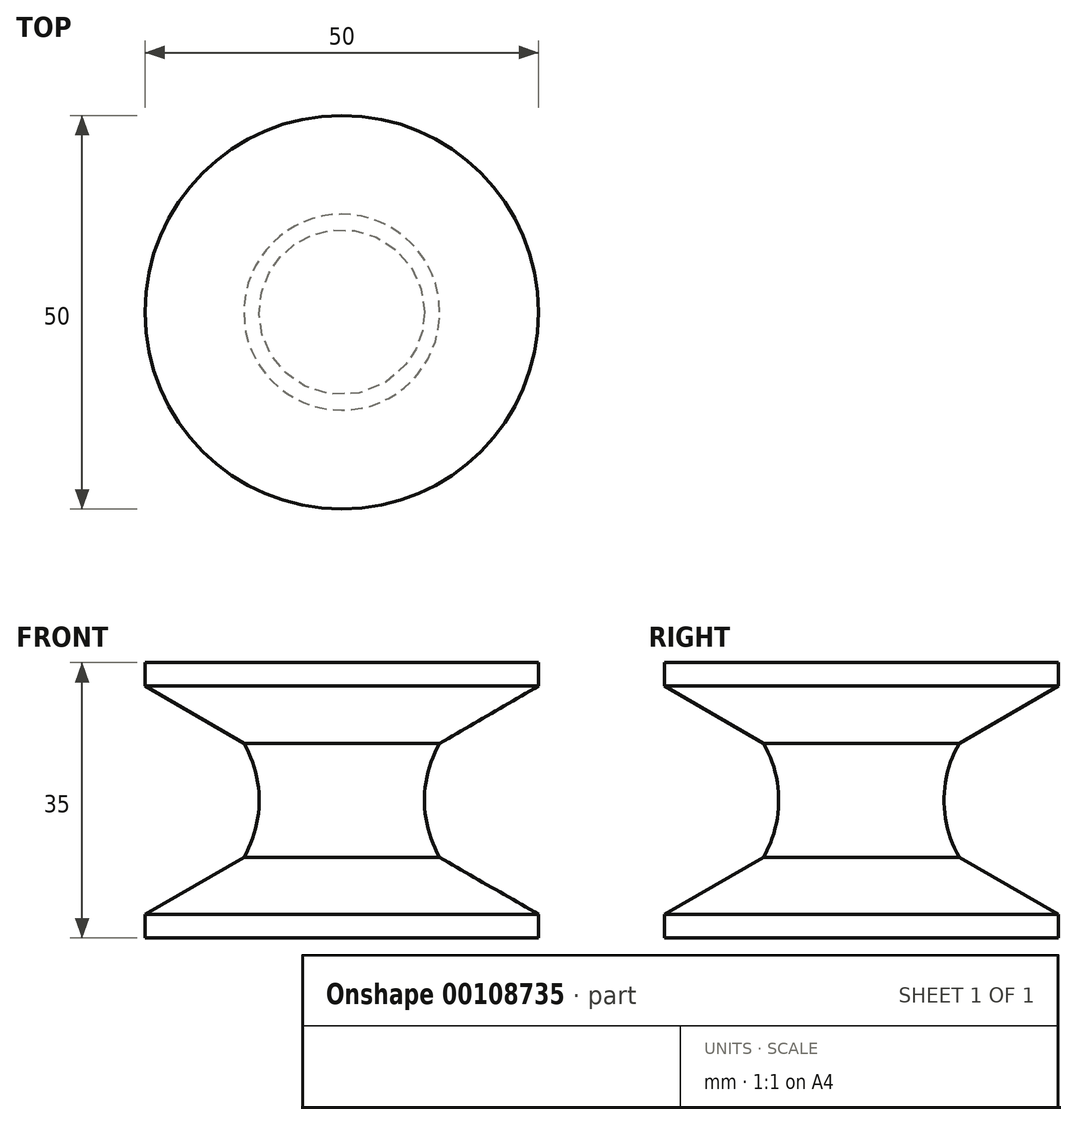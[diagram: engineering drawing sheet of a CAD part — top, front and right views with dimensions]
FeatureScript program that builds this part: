
annotation { "Feature Type Name" : "Feature", "Feature Type Description" : "" }
export const myFeature = defineFeature(function(context is Context, id is Id, definition is map)
    precondition{}
    {
        {
            var Q0;
            Q0=qCreatedBy(makeId("Top.planeOp"),FACE);
            var sketch = newSketch(context, id + "F0", { "sketchPlane" : qUnion([Q0])});
            skCircle(sketch, "E0", {"center": v(0, 0) * mm, "radius": 25 * mm});
            skSolve(sketch);
        }
        {
            var Q0;
            Q0=makeQuery(id+"F0.imprint","IMPRINT",FACE,{"disambiguationData":[TD([[makeQuery(id+"F0.imprint","IMPRINT",EDGE,{"derivedFrom":sQuery(id+"F0.wireOp",EDGE,"E0")}),1.0]])]});
            extrude(context, id + "F1", {"entities" : qUnion([Q0]), "depth" : 35 * mm});
        }
        {
            var Q0;
            Q0=qCreatedBy(makeId("Front.planeOp"),FACE);
            var sketch = newSketch(context, id + "F2", { "sketchPlane" : qUnion([Q0])});
            skLineSegment(sketch, "E1.0", {"start": v(-25, 35) * mm, "end": v(25, 35) * mm});
            skLineSegment(sketch, "E2.0", {"start": v(-25, 0) * mm, "end": v(25, 0) * mm});
            skLineSegment(sketch, "E3", {"start": v(-25, 0) * mm, "end": v(-25, 35) * mm});
            skLineSegment(sketch, "E4", {"start": v(25, 35) * mm, "end": v(25, 0) * mm});
            skLineSegment(sketch, "E5", {"start": v(0, 0) * mm, "end": v(0, 35) * mm});
            skLineSegment(sketch, "E6", {"start": v(-25, 32) * mm, "end": v(25, 32) * mm});
            skLineSegment(sketch, "E7", {"start": v(-25, 3) * mm, "end": v(25, 3) * mm});
            skArc(sketch, "E8", {"start": v(-25, 3) * mm, "mid": v(-10.5, 17.5) * mm, "end": v(-25, 32) * mm});
            skArc(sketch, "E9", {"start": v(-6, 35) * mm, "mid": v(0, 29) * mm, "end": v(6, 35) * mm});
            skArc(sketch, "E10", {"start": v(6, 0) * mm, "mid": v(0, 6) * mm, "end": v(-6, 0) * mm});
            skLineSegment(sketch, "E11", {"start": v(-25, 32) * mm, "end": v(-12.44, 24.75) * mm});
            skLineSegment(sketch, "E12", {"start": v(-25, 3) * mm, "end": v(-12.44, 10.25) * mm});
            skSolve(sketch);
        }
        {
            var Q0;
            {var subQ0=sQuery(id+"F2.wireOp",EDGE,"E11");Q0=makeQuery(id+"F2.imprint","IMPRINT",FACE,{"disambiguationData":[TD([[makeQuery(id+"F2.imprint","IMPRINT",EDGE,{"derivedFrom":subQ0}),-1.0]])]});}
            var Q1;
            Q1=sQuery(id+"F2.wireOp",EDGE,"E5");
            revolve(context, id + "F3", {"operationType" : NewBodyOperationType.REMOVE, "entities" : qUnion([Q0]), "axis" : qUnion([Q1]), "revolveType" : RevolveType.FULL, "oppositeDirection" : true});
        }
    });
